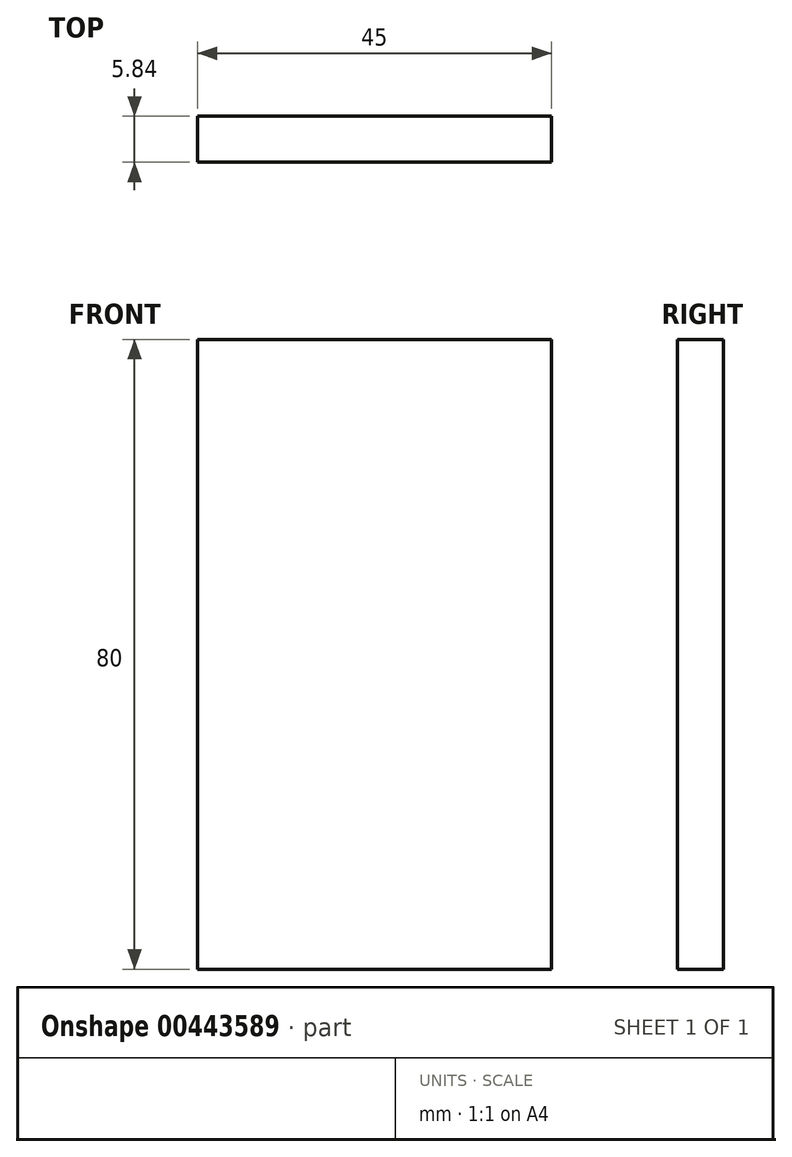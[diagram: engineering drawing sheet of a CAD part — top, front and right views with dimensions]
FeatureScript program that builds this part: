
annotation { "Feature Type Name" : "Feature", "Feature Type Description" : "" }
export const myFeature = defineFeature(function(context is Context, id is Id, definition is map)
    precondition{}
    {
        {
            var Q0;
            Q0=qCreatedBy(makeId("Front.planeOp"),FACE);
            var sketch = newSketch(context, id + "F0", { "sketchPlane" : qUnion([Q0])});
            skLineSegment(sketch, "E0.bottom", {"start": v(-22.7, 80) * mm, "end": v(22.3, 80) * mm});
            skLineSegment(sketch, "E0.top", {"start": v(-22.7, 0) * mm, "end": v(22.3, 0) * mm});
            skLineSegment(sketch, "E0.left", {"start": v(-22.7, 80) * mm, "end": v(-22.7, 0) * mm});
            skLineSegment(sketch, "E0.right", {"start": v(22.3, 80) * mm, "end": v(22.3, 0) * mm});
            skSolve(sketch);
        }
        {
            var Q0;
            Q0=makeQuery(id+"F0.imprint","IMPRINT",FACE,{"disambiguationData":[TD([[makeQuery(id+"F0.imprint","IMPRINT",EDGE,{"derivedFrom":sQuery(id+"F0.wireOp",EDGE,"E0.bottom")}),-1.0]])]});
            extrude(context, id + "F1", {"entities" : qUnion([Q0]), "depth" : 5.84 * mm});
        }
    });
